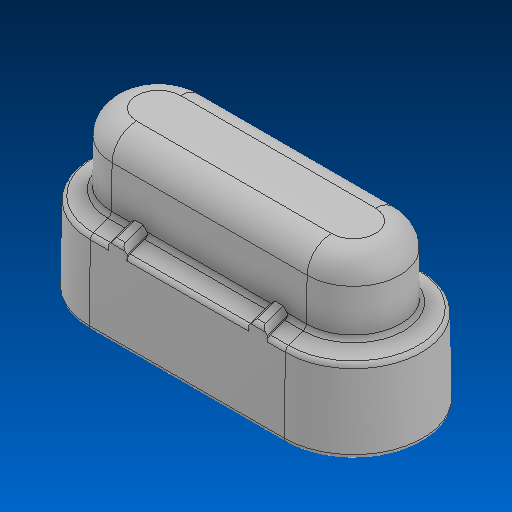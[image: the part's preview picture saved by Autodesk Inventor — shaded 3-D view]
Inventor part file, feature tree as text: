
AUTODESK INVENTOR PART (.ipt)
format: ipt  version: 2022.2 (Build 262287000, 287)  size: 541,696 bytes
history: native  units: in
note: dims shown in document units (in); Inventor stores cm internally (conversion verified against a paired STEP export)
features: fillet x1
ambient origin geometry x8: Origin, YZ Plane, XZ Plane, XY Plane, X Axis, Y Axis, Z Axis, Center Point
bodies: Solid1 (feature_tree)
feature tree (1):
  fillet  "Fillet3"  [1 undecoded]
note: 1 required parameter value undecoded (feature->parameter linkage not recoverable at this tier; creation-order binding heuristic only, values carry confidence <= 0.55)
